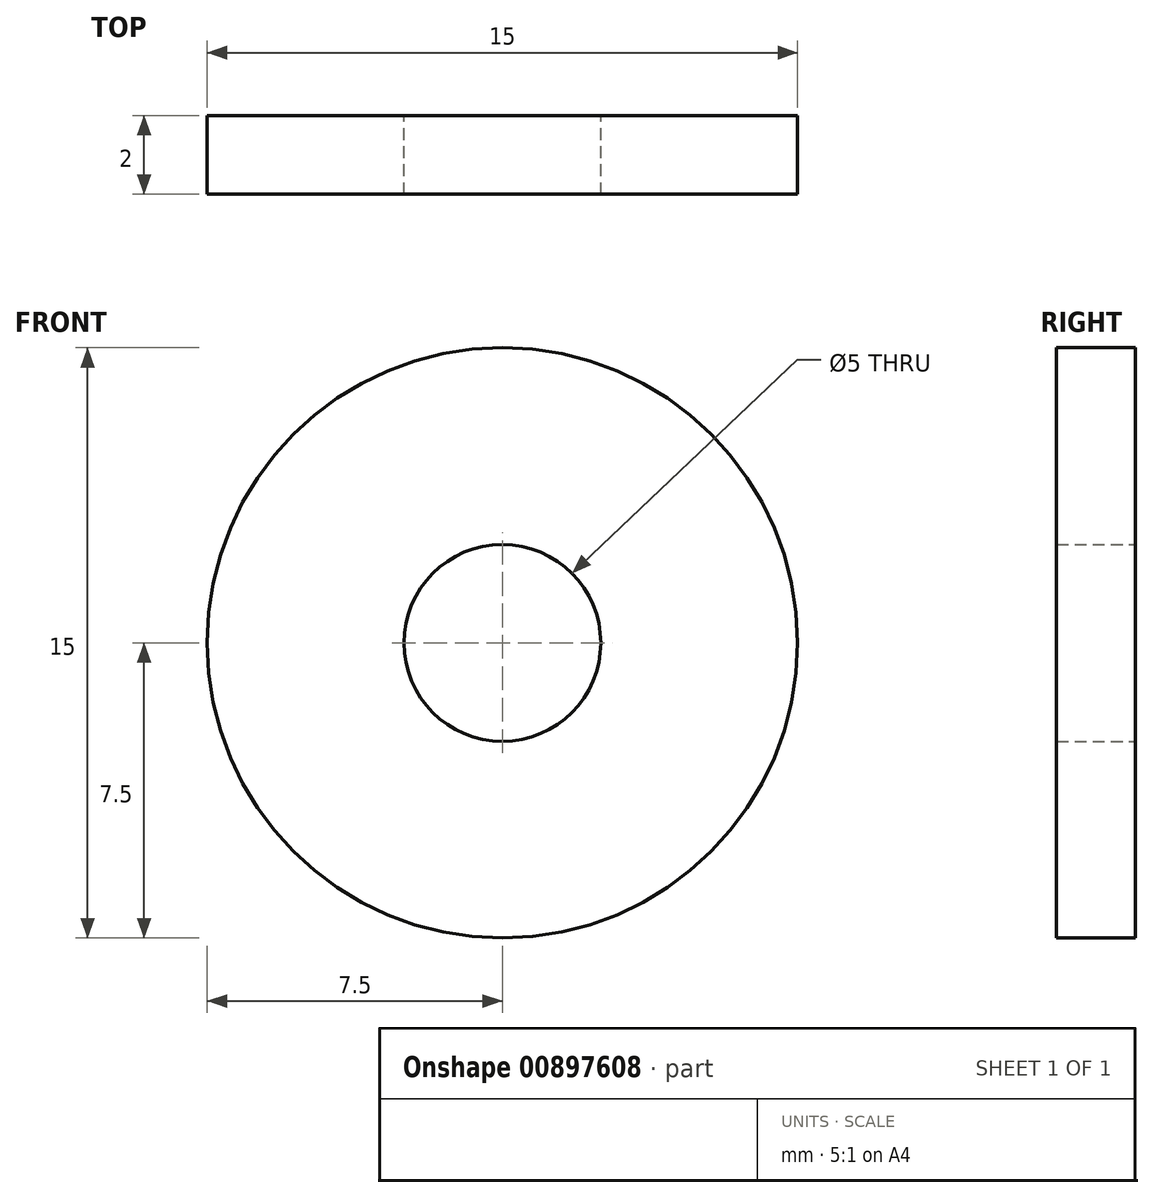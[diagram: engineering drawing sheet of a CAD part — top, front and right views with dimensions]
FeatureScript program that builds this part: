
annotation { "Feature Type Name" : "Feature", "Feature Type Description" : "" }
export const myFeature = defineFeature(function(context is Context, id is Id, definition is map)
    precondition{}
    {
        {
            var Q0;
            Q0=qCreatedBy(makeId("Front.planeOp"),FACE);
            var sketch = newSketch(context, id + "F0", { "sketchPlane" : qUnion([Q0])});
            skCircle(sketch, "E0", {"center": v(0, 0) * mm, "radius": 2.5 * mm});
            skCircle(sketch, "E1", {"center": v(0, 0) * mm, "radius": 7.5 * mm});
            skSolve(sketch);
        }
        {
            var Q0;
            Q0=makeQuery(id+"F0.imprint","IMPRINT",FACE,{"disambiguationData":[TD([[makeQuery(id+"F0.imprint","IMPRINT",EDGE,{"derivedFrom":sQuery(id+"F0.wireOp",EDGE,"E0")}),-1.0]])]});
            extrude(context, id + "F1", {"entities" : qUnion([Q0]), "depth" : 2 * mm, "offsetDistance" : 25 * mm, "symmetric" : true});
        }
    });
